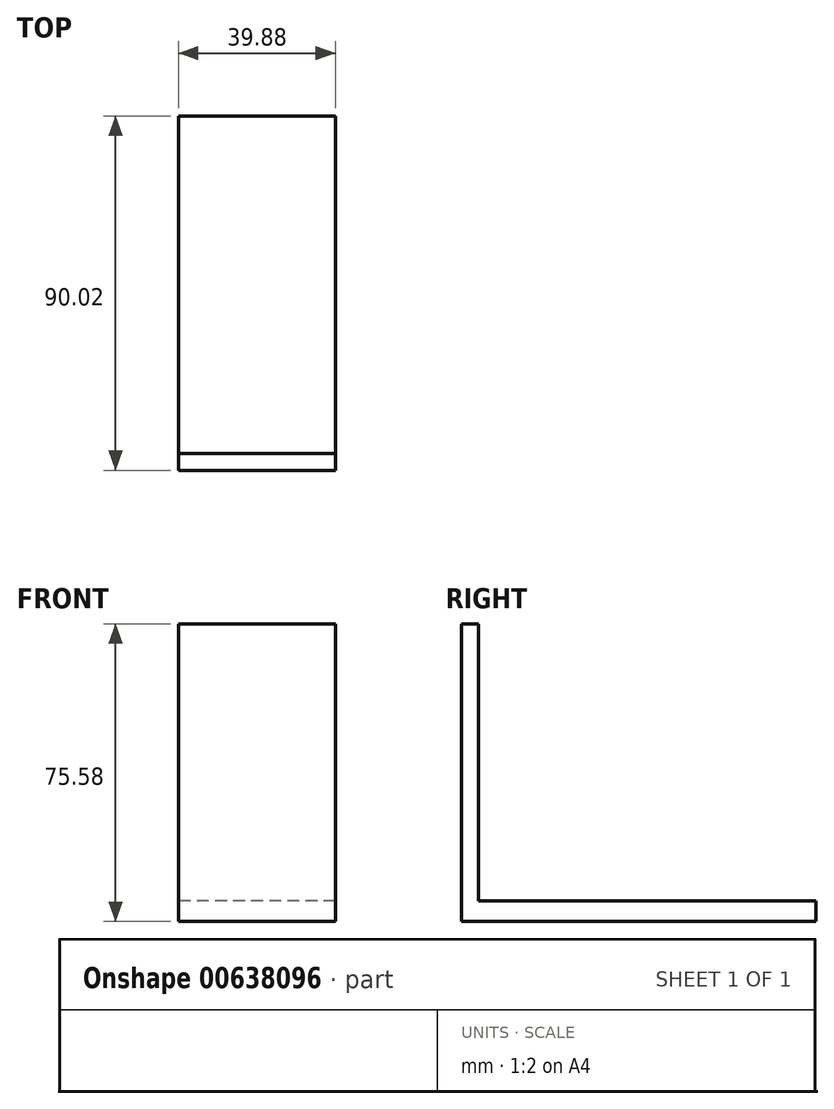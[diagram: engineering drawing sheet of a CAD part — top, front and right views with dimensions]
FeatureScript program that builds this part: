
annotation { "Feature Type Name" : "Feature", "Feature Type Description" : "" }
export const myFeature = defineFeature(function(context is Context, id is Id, definition is map)
    precondition{}
    {
        {
            var Q0;
            Q0=qCreatedBy(makeId("Right.planeOp"),FACE);
            var sketch = newSketch(context, id + "F0", { "sketchPlane" : qUnion([Q0])});
            skLineSegment(sketch, "E0", {"start": v(49.59, 0) * mm, "end": v(49.59, -5.15) * mm});
            skLineSegment(sketch, "E1", {"start": v(49.59, -5.15) * mm, "end": v(-40.43, -5.15) * mm});
            skLineSegment(sketch, "E2", {"start": v(-40.43, -5.15) * mm, "end": v(-40.43, 70.43) * mm});
            skLineSegment(sketch, "E3", {"start": v(-40.43, 70.43) * mm, "end": v(-36.08, 70.43) * mm});
            skLineSegment(sketch, "E4", {"start": v(-36.08, 70.43) * mm, "end": v(-36.08, 0) * mm});
            skLineSegment(sketch, "E5", {"start": v(-36.08, 0) * mm, "end": v(49.59, 0) * mm});
            skSolve(sketch);
        }
        {
            var Q0;
            Q0 = qSketchRegion(id + "F0", true);
            extrude(context, id + "F1", {"entities" : qUnion([Q0]), "depth" : 39.88 * mm, "offsetDistance" : 25.4 * mm});
        }
    });
